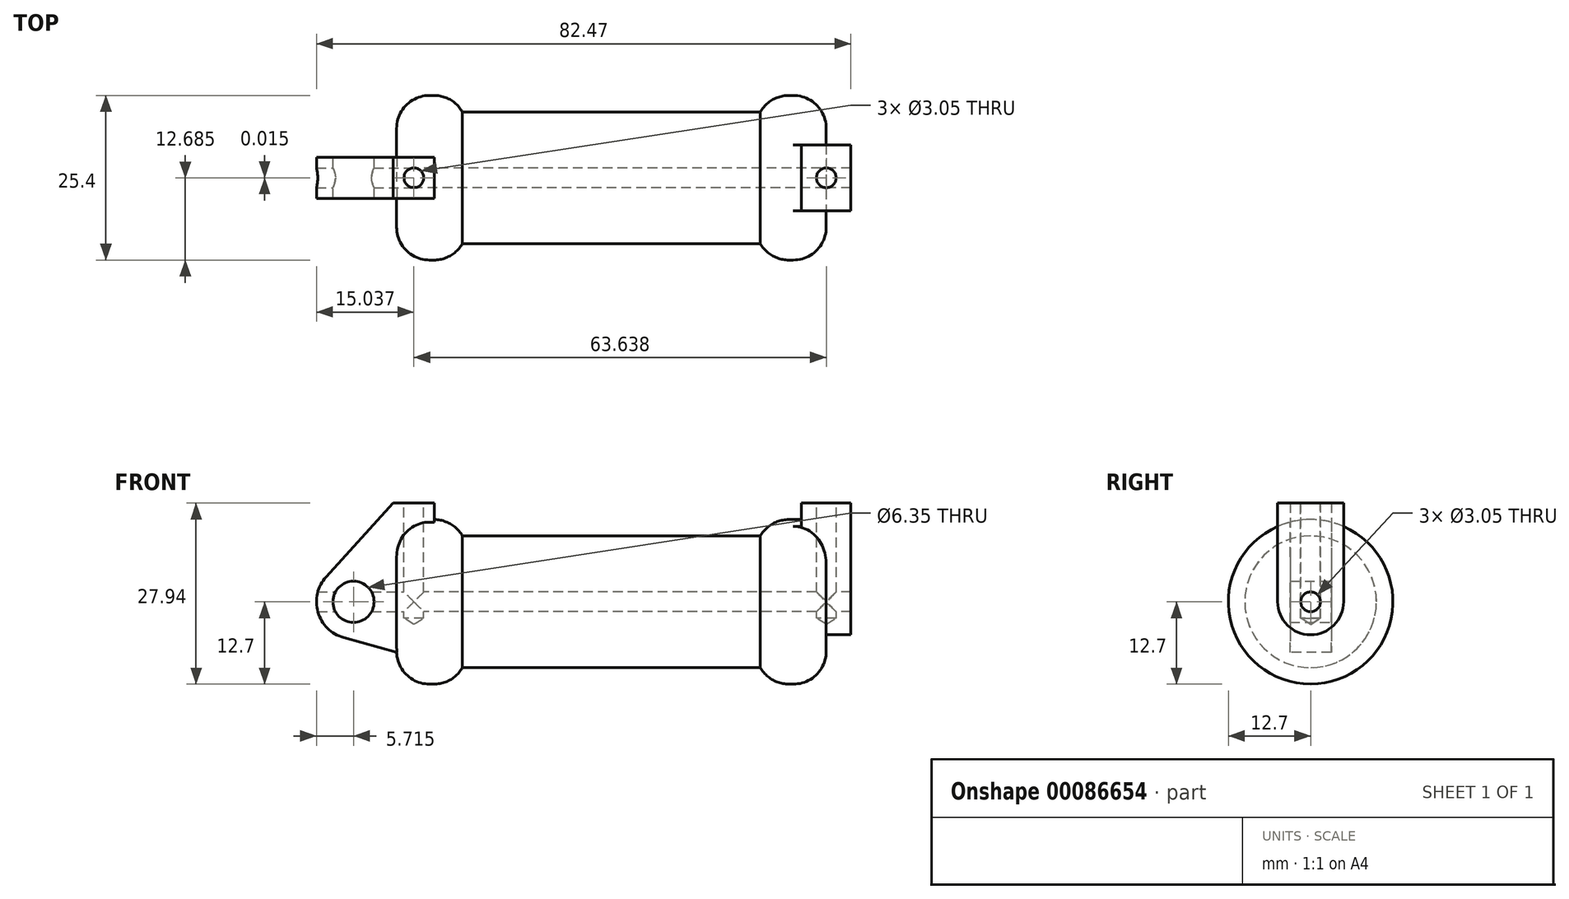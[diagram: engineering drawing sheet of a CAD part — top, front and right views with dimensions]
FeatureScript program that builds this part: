
annotation { "Feature Type Name" : "Feature", "Feature Type Description" : "" }
export const myFeature = defineFeature(function(context is Context, id is Id, definition is map)
    precondition{}
    {
        {
            var Q0;
            Q0=qCreatedBy(makeId("Front.planeOp"),FACE);
            var sketch = newSketch(context, id + "F0", { "sketchPlane" : qUnion([Q0])});
            skLineSegment(sketch, "E0", {"start": v(0, 0) * mm, "end": v(0, 12.7) * mm});
            skLineSegment(sketch, "E1", {"start": v(0, 12.7) * mm, "end": v(10.16, 12.7) * mm});
            skLineSegment(sketch, "E2", {"start": v(10.16, 12.7) * mm, "end": v(10.16, 10.16) * mm});
            skLineSegment(sketch, "E3", {"start": v(10.16, 10.16) * mm, "end": v(56.13, 10.16) * mm});
            skLineSegment(sketch, "E4", {"start": v(56.13, 10.16) * mm, "end": v(56.13, 12.7) * mm});
            skLineSegment(sketch, "E5", {"start": v(56.13, 12.7) * mm, "end": v(66.3, 12.7) * mm});
            skLineSegment(sketch, "E6", {"start": v(66.3, 12.7) * mm, "end": v(66.3, 0) * mm});
            skLineSegment(sketch, "E7", {"start": v(66.3, 0) * mm, "end": v(0, 0) * mm});
            skLineSegment(sketch, "E8", {"start": v(5.84, 15.24) * mm, "end": v(-0.5, 15.24) * mm});
            skLineSegment(sketch, "E9", {"start": v(-0.5, 15.24) * mm, "end": v(-10.88, 3.85) * mm});
            skLineSegment(sketch, "E10", {"start": v(0, 0) * mm, "end": v(-6.65, 0) * mm});
            skCircle(sketch, "E11", {"center": v(-6.65, 0) * mm, "radius": 5.72 * mm});
            skCircle(sketch, "E12", {"center": v(-6.65, 0) * mm, "radius": 3.18 * mm});
            skLineSegment(sketch, "E13", {"start": v(5.84, 15.24) * mm, "end": v(5.84, -9.4) * mm});
            skLineSegment(sketch, "E14", {"start": v(5.84, -9.4) * mm, "end": v(-8.18, -5.5) * mm});
            skSolve(sketch);
        }
        {
            var Q0;
            {var subQ0=sQuery(id+"F0.wireOp",EDGE,"E2");Q0=makeQuery(id+"F0.imprint","IMPRINT",FACE,{"disambiguationData":[TD([[makeQuery(id+"F0.imprint","IMPRINT",EDGE,{"derivedFrom":subQ0}),-1.0]])]});}
            var Q1;
            {var subQ0=sQuery(id+"F0.wireOp",EDGE,"E0");Q1=makeQuery(id+"F0.imprint","IMPRINT",FACE,{"disambiguationData":[TD([[makeQuery(id+"F0.imprint","IMPRINT",EDGE,{"derivedFrom":subQ0}),-1.0]])]});}
            var Q2;
            Q2=sQuery(id+"F0.wireOp",EDGE,"E7");
            revolve(context, id + "F1", {"entities" : qUnion([Q0, Q1]), "axis" : qUnion([Q2]), "revolveType" : RevolveType.FULL});
        }
        {
            var Q0;
            {var subQ0=sQuery(id+"F0.wireOp",EDGE,"E0");Q0=makeQuery(id+"F0.imprint","IMPRINT",FACE,{"disambiguationData":[TD([[makeQuery(id+"F0.imprint","IMPRINT",EDGE,{"derivedFrom":subQ0}),-1.0]])]});}
            var Q1;
            {var subQ3=sQuery(id+"F0.wireOp",EDGE,"E0");Q1=makeQuery(id+"F0.imprint","IMPRINT",FACE,{"disambiguationData":[TD([[makeQuery(id+"F0.imprint","IMPRINT",EDGE,{"derivedFrom":subQ3}),1.0]])]});}
            var Q2;
            {var subQ4=sQuery(id+"F0.wireOp",EDGE,"E12");Q2=makeQuery(id+"F0.imprint","IMPRINT",FACE,{"disambiguationData":[TD([[makeQuery(id+"F0.imprint","IMPRINT",EDGE,{"derivedFrom":subQ4}),-1.0]])]});}
            var Q3;
            {var subQ0=sQuery(id+"F0.wireOp",EDGE,"E14");Q3=makeQuery(id+"F0.imprint","IMPRINT",FACE,{"disambiguationData":[TD([[makeQuery(id+"F0.imprint","IMPRINT",EDGE,{"derivedFrom":subQ0}),-1.0]])]});}
            extrude(context, id + "F2", {"entities" : qUnion([Q0, Q1, Q2, Q3]), "operationType" : NewBodyOperationType.ADD, "endBound" : BoundingType.SYMMETRIC, "depth" : 6.35 * mm});
        }
        {
            var Q0;
            Q0=makeQuery(id+"F1.opRevolve","SWEPT_FACE",FACE,{"disambiguationData":[OSD([sQuery(id+"F0.wireOp",EDGE,"E6")])]});
            var sketch = newSketch(context, id + "F3", { "sketchPlane" : qUnion([Q0])});
            skCircle(sketch, "E15", {"center": v(0, 0) * mm, "radius": 1.52 * mm});
            skCircle(sketch, "E16", {"center": v(0, 0) * mm, "radius": 5.08 * mm});
            skLineSegment(sketch, "E17", {"start": v(5.08, 0) * mm, "end": v(5.08, 15.24) * mm});
            skLineSegment(sketch, "E18", {"start": v(-5.08, 0) * mm, "end": v(-5.08, 15.24) * mm});
            skLineSegment(sketch, "E19", {"start": v(-5.08, 15.24) * mm, "end": v(5.08, 15.24) * mm});
            skLineSegment(sketch, "E20", {"start": v(5.08, 0) * mm, "end": v(15.78, 0) * mm});
            skLineSegment(sketch, "E21", {"start": v(5.08, 15.24) * mm, "end": v(15.78, 15.24) * mm});
            skSolve(sketch);
        }
        {
            var Q0;
            Q0 = qSketchRegion(id + "F3", true);
            extrude(context, id + "F4", {"entities" : qUnion([Q0]), "operationType" : NewBodyOperationType.ADD, "endBound" : BoundingType.SYMMETRIC, "depth" : 7.62 * mm});
        }
        {
            var Q0;
            Q0=makeQuery(id+"F2.opExtrude","SWEPT_FACE",FACE,{"disambiguationData":[OSD([sQuery(id+"F0.wireOp",EDGE,"E8")])]});
            var sketch = newSketch(context, id + "F5", { "sketchPlane" : qUnion([Q0])});
            skCircle(sketch, "E22", {"center": v(2.67, 0) * mm, "radius": 1.52 * mm});
            skPoint(sketch, "E22.centerSnap0", {"position": v(-0.5, 0) * mm});
            skPoint(sketch, "E22.centerSnap1", {"position": v(2.67, -3.18) * mm});
            skSolve(sketch);
        }
        {
            var Q0;
            Q0=makeQuery(id+"F4.opExtrude","SWEPT_FACE",FACE,{"disambiguationData":[OSD([sQuery(id+"F3.wireOp",EDGE,"E19")])]});
            var sketch = newSketch(context, id + "F6", { "sketchPlane" : qUnion([Q0])});
            skCircle(sketch, "E23", {"center": v(66.3, -0.01) * mm, "radius": 1.52 * mm});
            skSolve(sketch);
        }
        {
            var Q0;
            Q0=sQuery(id+"F5.wireOp",VERTEX,"E22.center");
            var Q1;
            Q1=sQuery(id+"F6.wireOp",VERTEX,"E23.center");
            var Q2;
            Q2=makeQuery(id+"F1.opRevolve","SWEPT_BODY",BODY,{"disambiguationData":[OSD([sQuery(id+"F0.wireOp",EDGE,"E0"),sQuery(id+"F0.wireOp",EDGE,"E1"),sQuery(id+"F0.wireOp",EDGE,"E2"),sQuery(id+"F0.wireOp",EDGE,"E3"),sQuery(id+"F0.wireOp",EDGE,"E4"),sQuery(id+"F0.wireOp",EDGE,"E5"),sQuery(id+"F0.wireOp",EDGE,"E6"),sQuery(id+"F0.wireOp",EDGE,"E7")])]});
            hole(context, id + "F7", {"style" : HoleStyle.SIMPLE, "endStyle" : HoleEndStyle.BLIND, "holeDiameter" : 3.05 * mm, "holeDepth" : 17.78 * mm, "locations" : qUnion([Q0, Q1]), "scope" : qUnion([Q2])});
        }
        {
            var Q0;
            Q0=sQuery(id+"F3.wireOp",VERTEX,"E16.center");
            var Q1;
            Q1=makeQuery(id+"F1.opRevolve","SWEPT_BODY",BODY,{"disambiguationData":[OSD([sQuery(id+"F0.wireOp",EDGE,"E0"),sQuery(id+"F0.wireOp",EDGE,"E1"),sQuery(id+"F0.wireOp",EDGE,"E2"),sQuery(id+"F0.wireOp",EDGE,"E3"),sQuery(id+"F0.wireOp",EDGE,"E4"),sQuery(id+"F0.wireOp",EDGE,"E5"),sQuery(id+"F0.wireOp",EDGE,"E6"),sQuery(id+"F0.wireOp",EDGE,"E7")])]});
            hole(context, id + "F8", {"style" : HoleStyle.SIMPLE, "endStyle" : HoleEndStyle.THROUGH, "holeDiameter" : 3.05 * mm, "locations" : qUnion([Q0]), "scope" : qUnion([Q1]), "isTappedThrough" : true});
        }
        {
            var Q0;
            Q0=makeQuery(id+"F1.opRevolve","SWEPT_EDGE",EDGE,{"disambiguationData":[OSD([sQuery(id+"F0.wireOp",EDGE,"E4"),sQuery(id+"F0.wireOp",EDGE,"E5")])]});
            var Q1;
            Q1=makeQuery(id+"F1.opRevolve","SWEPT_EDGE",EDGE,{"disambiguationData":[OSD([sQuery(id+"F0.wireOp",EDGE,"E1"),sQuery(id+"F0.wireOp",EDGE,"E2")])]});
            var Q2;
            Q2=makeQuery(id+"F1.opRevolve","SWEPT_EDGE",EDGE,{"disambiguationData":[OSD([sQuery(id+"F0.wireOp",EDGE,"E0"),sQuery(id+"F0.wireOp",EDGE,"E1")])]});
            var Q3;
            Q3=makeQuery(id+"F1.opRevolve","SWEPT_EDGE",EDGE,{"disambiguationData":[OSD([sQuery(id+"F0.wireOp",EDGE,"E5"),sQuery(id+"F0.wireOp",EDGE,"E6")])]});
            fillet(context, id + "F9", {"entities" : qUnion([Q0, Q1, Q2, Q3]), "radius" : 5.08 * mm, "tangentPropagation" : true, "allowEdgeOverflow" : false});
        }
    });
